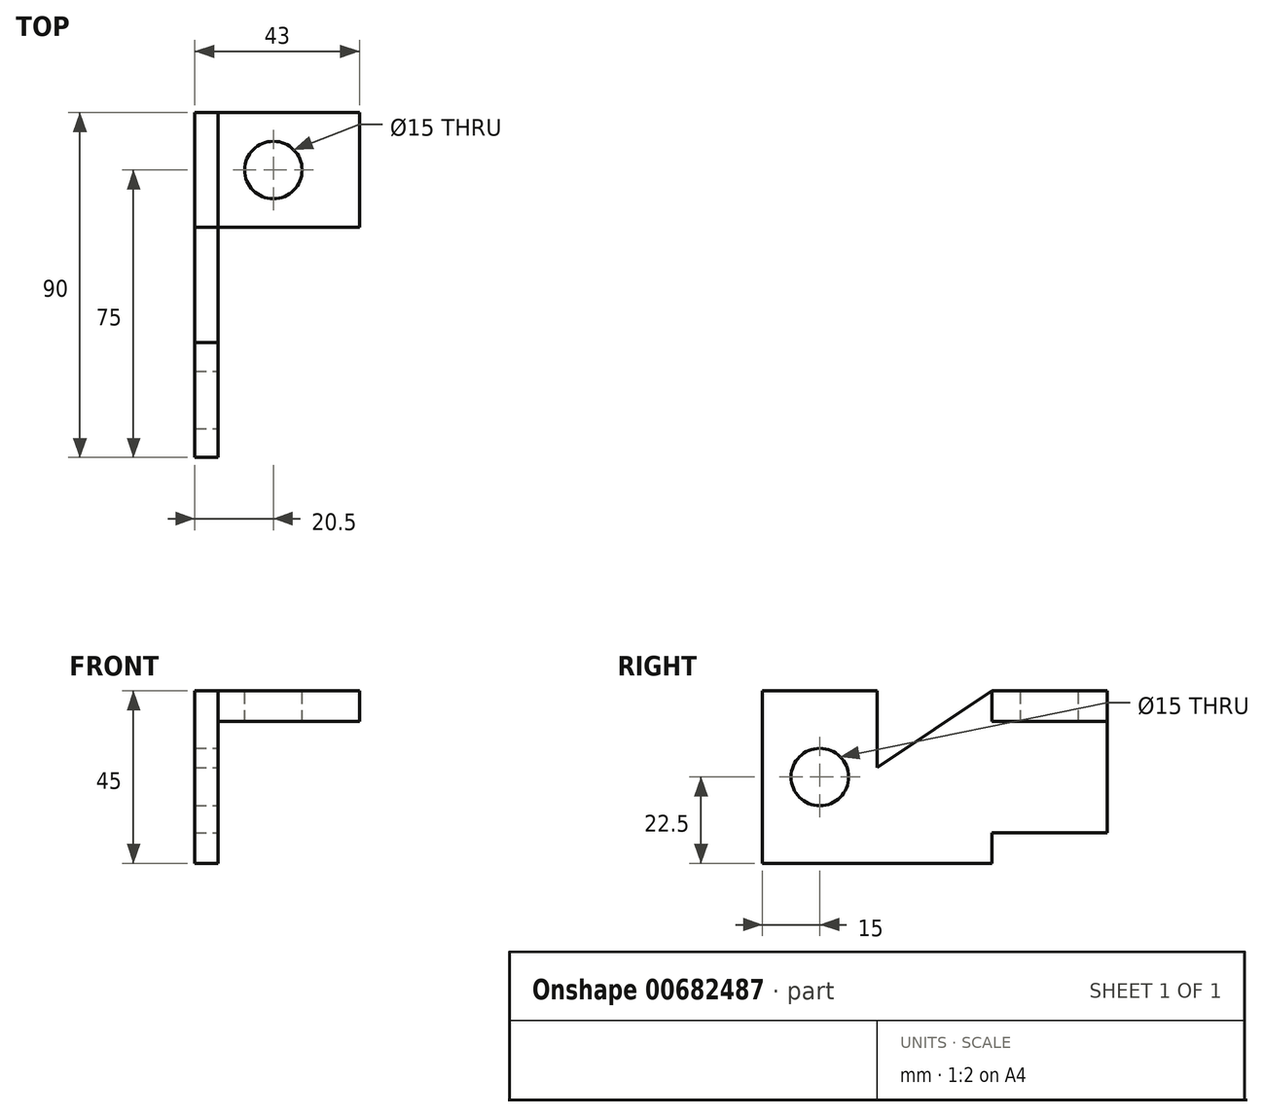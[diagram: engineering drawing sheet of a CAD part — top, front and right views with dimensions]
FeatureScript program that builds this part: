
annotation { "Feature Type Name" : "Feature", "Feature Type Description" : "" }
export const myFeature = defineFeature(function(context is Context, id is Id, definition is map)
    precondition{}
    {
        {
            var Q0;
            Q0=qCreatedBy(makeId("Right.planeOp"),FACE);
            var sketch = newSketch(context, id + "F0", { "sketchPlane" : qUnion([Q0])});
            skLineSegment(sketch, "E0", {"start": v(0, 0) * mm, "end": v(0, 45) * mm});
            skLineSegment(sketch, "E1", {"start": v(0, 45) * mm, "end": v(30, 45) * mm});
            skLineSegment(sketch, "E2", {"start": v(30, 45) * mm, "end": v(30, 25) * mm});
            skLineSegment(sketch, "E3", {"start": v(30, 25) * mm, "end": v(60, 45) * mm});
            skLineSegment(sketch, "E4", {"start": v(60, 45) * mm, "end": v(90, 45) * mm});
            skLineSegment(sketch, "E5", {"start": v(90, 45) * mm, "end": v(90, 0) * mm});
            skLineSegment(sketch, "E6", {"start": v(90, 0) * mm, "end": v(0, 0) * mm});
            skLineSegment(sketch, "E7.top", {"start": v(60, 37) * mm, "end": v(90, 37) * mm});
            skLineSegment(sketch, "E7.left", {"start": v(60, 45) * mm, "end": v(60, 37) * mm});
            skLineSegment(sketch, "E7.right", {"start": v(90, 45) * mm, "end": v(90, 37) * mm});
            skLineSegment(sketch, "E8.bottom", {"start": v(90, 0) * mm, "end": v(60, 0) * mm});
            skLineSegment(sketch, "E8.top", {"start": v(90, 8) * mm, "end": v(60, 8) * mm});
            skLineSegment(sketch, "E8.left", {"start": v(90, 0) * mm, "end": v(90, 8) * mm});
            skLineSegment(sketch, "E8.right", {"start": v(60, 0) * mm, "end": v(60, 8) * mm});
            skSolve(sketch);
        }
        {
            var Q0;
            Q0=makeQuery(id+"F0.imprint","IMPRINT",FACE,{"disambiguationData":[TD([[makeQuery(id+"F0.imprint","IMPRINT",EDGE,{"derivedFrom":sQuery(id+"F0.wireOp",EDGE,"E0")}),-1.0]])]});
            var Q1;
            Q1=makeQuery(id+"F2.opExtrude","CAP_FACE",FACE,{"disambiguationData":[OSD([sQuery(id+"F0.wireOp",EDGE,"E4"),sQuery(id+"F0.wireOp",EDGE,"E7.top"),sQuery(id+"F0.wireOp",EDGE,"E7.left"),sQuery(id+"F0.wireOp",EDGE,"E7.right")])],"isStart":true});
            var Q2;
            Q2=makeQuery(id+"F2.opExtrude","CAP_FACE",FACE,{"disambiguationData":[OSD([sQuery(id+"F0.wireOp",EDGE,"E8.bottom"),sQuery(id+"F0.wireOp",EDGE,"E8.top"),sQuery(id+"F0.wireOp",EDGE,"E8.left"),sQuery(id+"F0.wireOp",EDGE,"E8.right")])],"isStart":true});
            var Q3;
            Q3=makeQuery(id+"F0.imprint","IMPRINT",FACE,{"disambiguationData":[TD([[makeQuery(id+"F0.imprint","IMPRINT",EDGE,{"derivedFrom":sQuery(id+"F0.wireOp",EDGE,"E4")}),-1.0]])]});
            var Q4;
            Q4=makeQuery(id+"F0.imprint","IMPRINT",FACE,{"disambiguationData":[TD([[makeQuery(id+"F0.imprint","IMPRINT",EDGE,{"derivedFrom":sQuery(id+"F0.wireOp",EDGE,"E8.bottom")}),-1.0]])]});
            extrude(context, id + "F1", {"entities" : qUnion([Q0, Q1, Q2, Q3, Q4]), "oppositeDirection" : true, "depth" : 6 * mm, "offsetDistance" : 25 * mm});
        }
        {
            var Q0;
            Q0=makeQuery(id+"F0.imprint","IMPRINT",FACE,{"disambiguationData":[TD([[makeQuery(id+"F0.imprint","IMPRINT",EDGE,{"derivedFrom":sQuery(id+"F0.wireOp",EDGE,"E4")}),-1.0]])]});
            var Q1;
            Q1=makeQuery(id+"F0.imprint","IMPRINT",FACE,{"disambiguationData":[TD([[makeQuery(id+"F0.imprint","IMPRINT",EDGE,{"derivedFrom":sQuery(id+"F0.wireOp",EDGE,"E8.bottom")}),-1.0]])]});
            extrude(context, id + "F2", {"entities" : qUnion([Q0, Q1]), "depth" : 37 * mm, "offsetDistance" : 25 * mm});
        }
        {
            var Q0;
            Q0=makeQuery(id+"F2.opExtrude","SWEPT_FACE",FACE,{"disambiguationData":[OSD([sQuery(id+"F0.wireOp",EDGE,"E4")])]});
            var sketch = newSketch(context, id + "F3", { "sketchPlane" : qUnion([Q0])});
            skCircle(sketch, "E9", {"center": v(14.5, 75) * mm, "radius": 7.5 * mm});
            skSolve(sketch);
        }
        {
            var Q0;
            Q0=sQuery(id+"F3.wireOp",VERTEX,"E9.center");
            var Q1;
            Q1=makeQuery(id+"F2.opExtrude","SWEPT_BODY",BODY,{"disambiguationData":[OSD([sQuery(id+"F0.wireOp",EDGE,"E4"),sQuery(id+"F0.wireOp",EDGE,"E7.top"),sQuery(id+"F0.wireOp",EDGE,"E7.left"),sQuery(id+"F0.wireOp",EDGE,"E7.right")])]});
            var Q2;
            Q2=makeQuery(id+"F2.opExtrude","SWEPT_BODY",BODY,{"disambiguationData":[OSD([sQuery(id+"F0.wireOp",EDGE,"E8.bottom"),sQuery(id+"F0.wireOp",EDGE,"E8.top"),sQuery(id+"F0.wireOp",EDGE,"E8.left"),sQuery(id+"F0.wireOp",EDGE,"E8.right")])]});
            hole(context, id + "F4", {"style" : HoleStyle.SIMPLE, "endStyle" : HoleEndStyle.THROUGH, "holeDiameter" : 15 * mm, "majorDiameter" : 5 * mm, "isTappedThrough" : true, "tappedDepth" : 12 * mm, "tapClearance" : 3, "locations" : qUnion([Q0]), "scope" : qUnion([Q1, Q2])});
        }
        {
            var Q0;
            Q0=makeQuery(id+"F1.opExtrude","CAP_FACE",FACE,{"disambiguationData":[OSD([sQuery(id+"F0.wireOp",EDGE,"E0"),sQuery(id+"F0.wireOp",EDGE,"E1"),sQuery(id+"F0.wireOp",EDGE,"E2"),sQuery(id+"F0.wireOp",EDGE,"E3"),sQuery(id+"F0.wireOp",EDGE,"E5"),sQuery(id+"F0.wireOp",EDGE,"E6"),sQuery(id+"F0.wireOp",EDGE,"E4"),sQuery(id+"F0.wireOp",EDGE,"E7.right"),sQuery(id+"F0.wireOp",EDGE,"E8.bottom"),sQuery(id+"F0.wireOp",EDGE,"E8.left")])],"isStart":true});
            var sketch = newSketch(context, id + "F5", { "sketchPlane" : qUnion([Q0])});
            skLineSegment(sketch, "E10", {"start": v(0, 0) * mm, "end": v(0, 22.5) * mm});
            skLineSegment(sketch, "E11", {"start": v(15, 45) * mm, "end": v(15, 22.5) * mm});
            skSolve(sketch);
        }
        {
            var Q0;
            Q0=sQuery(id+"F5.wireOp",VERTEX,"E11.end");
            var Q1;
            Q1=makeQuery(id+"F1.opExtrude","SWEPT_BODY",BODY,{"disambiguationData":[OSD([sQuery(id+"F0.wireOp",EDGE,"E0"),sQuery(id+"F0.wireOp",EDGE,"E1"),sQuery(id+"F0.wireOp",EDGE,"E2"),sQuery(id+"F0.wireOp",EDGE,"E3"),sQuery(id+"F0.wireOp",EDGE,"E5"),sQuery(id+"F0.wireOp",EDGE,"E6"),sQuery(id+"F0.wireOp",EDGE,"E4"),sQuery(id+"F0.wireOp",EDGE,"E7.right"),sQuery(id+"F0.wireOp",EDGE,"E8.bottom"),sQuery(id+"F0.wireOp",EDGE,"E8.left")])]});
            hole(context, id + "F6", {"style" : HoleStyle.SIMPLE, "endStyle" : HoleEndStyle.THROUGH, "holeDiameter" : 15 * mm, "majorDiameter" : 5 * mm, "isTappedThrough" : true, "tappedDepth" : 12 * mm, "tapClearance" : 3, "locations" : qUnion([Q0]), "scope" : qUnion([Q1])});
        }
    });
